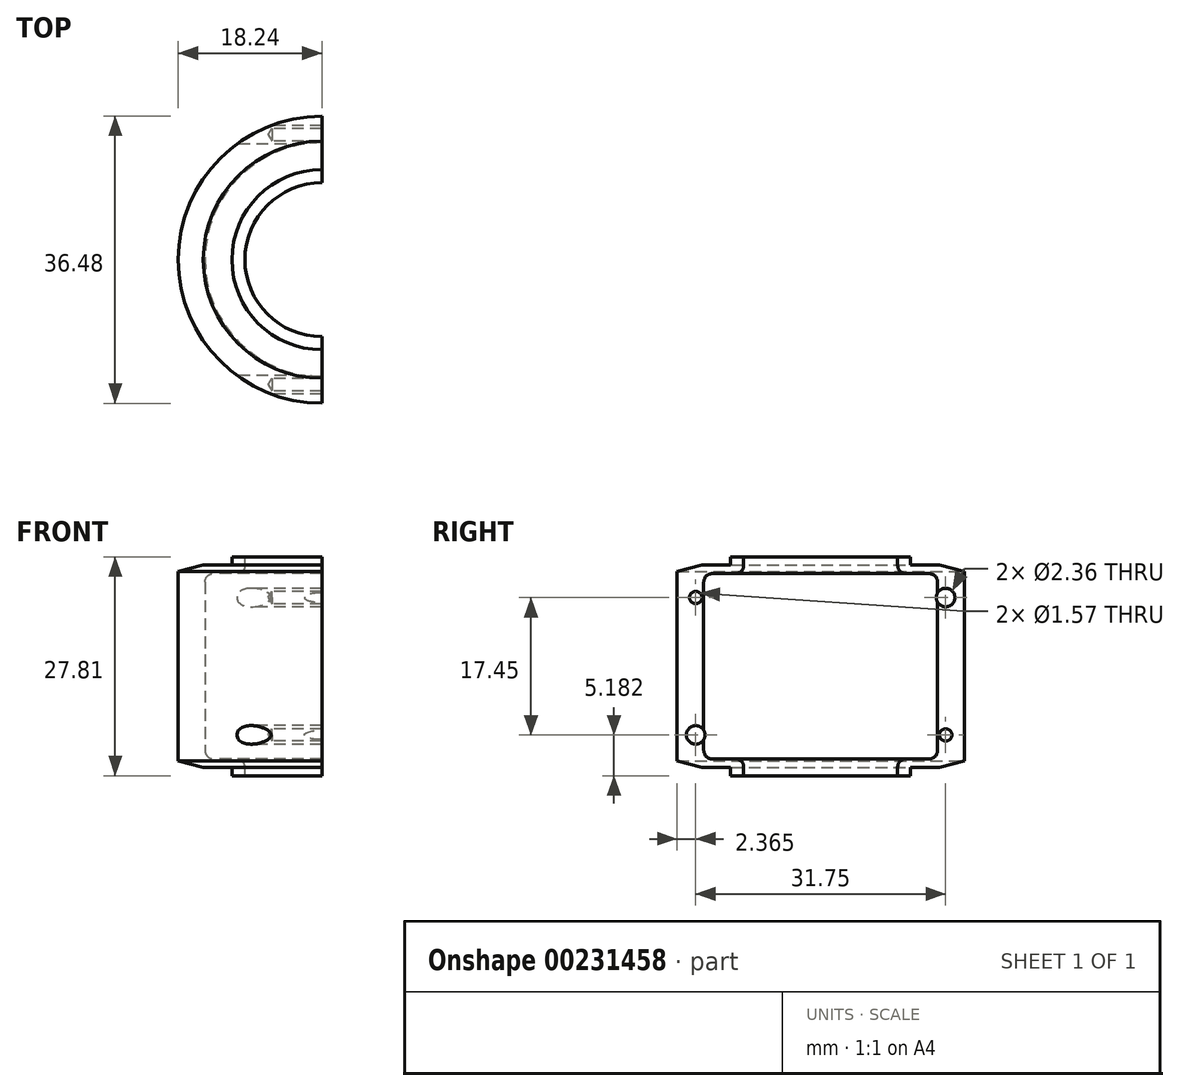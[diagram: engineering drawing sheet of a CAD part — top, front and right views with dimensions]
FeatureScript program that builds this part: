
annotation { "Feature Type Name" : "Feature", "Feature Type Description" : "" }
export const myFeature = defineFeature(function(context is Context, id is Id, definition is map)
    precondition{}
    {
        {
            var Q0;
            Q0=qCreatedBy(makeId("Right.planeOp"),FACE);
            var sketch = newSketch(context, id + "F0", { "sketchPlane" : qUnion([Q0])});
            skLineSegment(sketch, "E0", {"start": v(0, 0) * mm, "end": v(0, 2.13) * mm});
            skLineSegment(sketch, "E1", {"start": v(11.43, 0) * mm, "end": v(11.43, 1.04) * mm});
            skLineSegment(sketch, "E2", {"start": v(18.24, 1.04) * mm, "end": v(18.24, 26.77) * mm});
            skLineSegment(sketch, "E3", {"start": v(11.43, 1.04) * mm, "end": v(18.24, 1.04) * mm});
            skLineSegment(sketch, "E4", {"start": v(11.43, 26.77) * mm, "end": v(18.24, 26.77) * mm});
            skLineSegment(sketch, "E5", {"start": v(11.43, 26.77) * mm, "end": v(11.43, 27.81) * mm});
            skLineSegment(sketch, "E6", {"start": v(11.43, 27.81) * mm, "end": v(0, 27.81) * mm});
            skLineSegment(sketch, "E7", {"start": v(11.43, 0) * mm, "end": v(0, 0) * mm});
            skLineSegment(sketch, "E8", {"start": v(0, 2.13) * mm, "end": v(14.86, 2.13) * mm});
            skLineSegment(sketch, "E9", {"start": v(14.86, 2.13) * mm, "end": v(14.86, 25.68) * mm});
            skLineSegment(sketch, "E10", {"start": v(14.86, 25.68) * mm, "end": v(0, 25.68) * mm});
            skLineSegment(sketch, "E11.trimOffspring", {"start": v(0, 25.68) * mm, "end": v(0, 27.81) * mm});
            skSolve(sketch);
        }
        {
            var Q0;
            Q0=makeQuery(id+"F0.imprint","IMPRINT",FACE,{"disambiguationData":[TD([[makeQuery(id+"F0.imprint","IMPRINT",EDGE,{"derivedFrom":sQuery(id+"F0.wireOp",EDGE,"E0")}),-1.0]])]});
            var Q1;
            Q1=sQuery(id+"F0.wireOp",EDGE,"E11.trimOffspring");
            revolve(context, id + "F1", {"entities" : qUnion([Q0]), "axis" : qUnion([Q1]), "revolveType" : RevolveType.ONE_DIRECTION, "angle" : 180 * degree});
        }
        {
            var Q0;
            Q0=makeQuery(id+"F1.opRevolve","SWEPT_FACE",FACE,{"disambiguationData":[OSD([sQuery(id+"F0.wireOp",EDGE,"E6")])]});
            var sketch = newSketch(context, id + "F2", { "sketchPlane" : qUnion([Q0])});
            skCircle(sketch, "E12", {"center": v(0, 0) * mm, "radius": 9.78 * mm});
            skSolve(sketch);
        }
        {
            var Q0;
            {var subQ0=sQuery(id+"F2.wireOp",EDGE,"E12");var subQ1=makeQuery(id+"F1.opRevolve","CAP_EDGE",EDGE,{"disambiguationData":[OSD([sQuery(id+"F0.wireOp",EDGE,"E6")])],"isStart":false});var subQ2=makeQuery(id+"F2.imprint","INTERSECT",VERTEX,{"disambiguationData":[OD(0.0)],"derivedFrom":[subQ1,subQ0]});Q0=makeQuery(id+"F2.imprint","IMPRINT",FACE,{"disambiguationData":[TD([[makeQuery(id+"F2.imprint","IMPRINT",EDGE,{"disambiguationData":[TD([[subQ2,-1.0]])],"derivedFrom":subQ0}),1.0]])]});}
            var Q1;
            {var subQ0=sQuery(id+"F2.wireOp",EDGE,"E12");var subQ1=makeQuery(id+"F1.opRevolve","CAP_EDGE",EDGE,{"disambiguationData":[OSD([sQuery(id+"F0.wireOp",EDGE,"E6")])],"isStart":false});var subQ2=makeQuery(id+"F2.imprint","INTERSECT",VERTEX,{"disambiguationData":[OD(0.0)],"derivedFrom":[subQ1,subQ0]});Q1=makeQuery(id+"F2.imprint","IMPRINT",FACE,{"disambiguationData":[TD([[makeQuery(id+"F2.imprint","IMPRINT",EDGE,{"disambiguationData":[TD([[subQ2,1.0]])],"derivedFrom":subQ0}),1.0]])]});}
            extrude(context, id + "F3", {"entities" : qUnion([Q0, Q1]), "operationType" : NewBodyOperationType.REMOVE, "oppositeDirection" : true, "depth" : 27.8 * mm});
        }
        {
            var Q0;
            Q0=makeQuery(id+"F3.boolean.opBoolean","COPY",EDGE,{"derivedFrom":makeQuery(id+"F3.opExtrude","CAP_EDGE",EDGE,{"disambiguationData":[OSD([sQuery(id+"F2.wireOp",EDGE,"E12")])],"isStart":true})});
            var Q1;
            Q1=makeQuery(id+"F3.boolean.opBoolean","INTERSECT",EDGE,{"derivedFrom":[makeQuery(id+"F1.opRevolve","SWEPT_FACE",FACE,{"disambiguationData":[OSD([sQuery(id+"F0.wireOp",EDGE,"E10")])]}),makeQuery(id+"F3.opExtrude","SWEPT_FACE",FACE,{"disambiguationData":[OSD([sQuery(id+"F2.wireOp",EDGE,"E12")])]})]});
            var Q2;
            Q2=makeQuery(id+"F3.boolean.opBoolean","INTERSECT",EDGE,{"derivedFrom":[makeQuery(id+"F1.opRevolve","SWEPT_FACE",FACE,{"disambiguationData":[OSD([sQuery(id+"F0.wireOp",EDGE,"E8")])]}),makeQuery(id+"F3.opExtrude","SWEPT_FACE",FACE,{"disambiguationData":[OSD([sQuery(id+"F2.wireOp",EDGE,"E12")])]})]});
            var Q3;
            Q3=makeQuery(id+"F3.boolean.opBoolean","COPY",EDGE,{"derivedFrom":makeQuery(id+"F3.opExtrude","CAP_EDGE",EDGE,{"disambiguationData":[OSD([sQuery(id+"F2.wireOp",EDGE,"E12")])],"isStart":false})});
            fillet(context, id + "F4", {"entities" : qUnion([Q0, Q1, Q2, Q3]), "radius" : 1.02 * mm, "tangentPropagation" : true, "allowEdgeOverflow" : false});
        }
        {
            var Q0;
            Q0=makeQuery(id+"F1.opRevolve","SWEPT_EDGE",EDGE,{"disambiguationData":[OSD([sQuery(id+"F0.wireOp",EDGE,"E9"),sQuery(id+"F0.wireOp",EDGE,"E10")])]});
            var Q1;
            Q1=makeQuery(id+"F1.opRevolve","SWEPT_EDGE",EDGE,{"disambiguationData":[OSD([sQuery(id+"F0.wireOp",EDGE,"E8"),sQuery(id+"F0.wireOp",EDGE,"E9")])]});
            fillet(context, id + "F5", {"entities" : qUnion([Q0, Q1]), "radius" : 1.1 * mm, "tangentPropagation" : true, "allowEdgeOverflow" : false});
        }
        {
            var Q0;
            Q0=makeQuery(id+"F3.boolean.opBoolean","SPLIT",FACE,{"disambiguationData":[OD(0.0)],"derivedFrom":makeQuery(id+"F1.opRevolve","CAP_FACE",FACE,{"disambiguationData":[OSD([sQuery(id+"F0.wireOp",EDGE,"E0"),sQuery(id+"F0.wireOp",EDGE,"E1"),sQuery(id+"F0.wireOp",EDGE,"E2"),sQuery(id+"F0.wireOp",EDGE,"E3"),sQuery(id+"F0.wireOp",EDGE,"E4"),sQuery(id+"F0.wireOp",EDGE,"E5"),sQuery(id+"F0.wireOp",EDGE,"E6"),sQuery(id+"F0.wireOp",EDGE,"E7"),sQuery(id+"F0.wireOp",EDGE,"E8"),sQuery(id+"F0.wireOp",EDGE,"E9"),sQuery(id+"F0.wireOp",EDGE,"E10"),sQuery(id+"F0.wireOp",EDGE,"E11.trimOffspring")])],"isStart":false})});
            var sketch = newSketch(context, id + "F6", { "sketchPlane" : qUnion([Q0])});
            skPoint(sketch, "E13.startSnap0", {"position": v(18.24, 13.9) * mm});
            skPoint(sketch, "E14", {"position": v(15.88, 22.63) * mm});
            skPoint(sketch, "E15", {"position": v(15.88, 5.18) * mm});
            skPoint(sketch, "E16", {"position": v(-15.88, 5.18) * mm});
            skPoint(sketch, "E17", {"position": v(-15.88, 22.63) * mm});
            skSolve(sketch);
        }
        {
            var Q0;
            Q0=sQuery(id+"F6.wireOp",VERTEX,"E14");
            var Q1;
            Q1=sQuery(id+"F6.wireOp",VERTEX,"E16");
            var Q2;
            Q2=makeQuery(id+"F1.opRevolve","SWEPT_BODY",BODY,{"disambiguationData":[OSD([sQuery(id+"F0.wireOp",EDGE,"E0"),sQuery(id+"F0.wireOp",EDGE,"E1"),sQuery(id+"F0.wireOp",EDGE,"E2"),sQuery(id+"F0.wireOp",EDGE,"E3"),sQuery(id+"F0.wireOp",EDGE,"E4"),sQuery(id+"F0.wireOp",EDGE,"E5"),sQuery(id+"F0.wireOp",EDGE,"E6"),sQuery(id+"F0.wireOp",EDGE,"E7"),sQuery(id+"F0.wireOp",EDGE,"E8"),sQuery(id+"F0.wireOp",EDGE,"E9"),sQuery(id+"F0.wireOp",EDGE,"E10"),sQuery(id+"F0.wireOp",EDGE,"E11.trimOffspring")])]});
            hole(context, id + "F7", {"style" : HoleStyle.SIMPLE, "endStyle" : HoleEndStyle.THROUGH, "holeDiameter" : 2.36 * mm, "majorDiameter" : 6.35 * mm, "locations" : qUnion([Q0, Q1]), "scope" : qUnion([Q2]), "isTappedThrough" : true, "tappedDepth" : 12.7 * mm, "tapClearance" : 3});
        }
        {
            var Q0;
            Q0=sQuery(id+"F6.wireOp",VERTEX,"E15");
            var Q1;
            Q1=sQuery(id+"F6.wireOp",VERTEX,"E17");
            var Q2;
            Q2=makeQuery(id+"F1.opRevolve","SWEPT_BODY",BODY,{"disambiguationData":[OSD([sQuery(id+"F0.wireOp",EDGE,"E0"),sQuery(id+"F0.wireOp",EDGE,"E1"),sQuery(id+"F0.wireOp",EDGE,"E2"),sQuery(id+"F0.wireOp",EDGE,"E3"),sQuery(id+"F0.wireOp",EDGE,"E4"),sQuery(id+"F0.wireOp",EDGE,"E5"),sQuery(id+"F0.wireOp",EDGE,"E6"),sQuery(id+"F0.wireOp",EDGE,"E7"),sQuery(id+"F0.wireOp",EDGE,"E8"),sQuery(id+"F0.wireOp",EDGE,"E9"),sQuery(id+"F0.wireOp",EDGE,"E10"),sQuery(id+"F0.wireOp",EDGE,"E11.trimOffspring")])]});
            hole(context, id + "F8", {"style" : HoleStyle.SIMPLE, "endStyle" : HoleEndStyle.BLIND, "holeDiameter" : 1.57 * mm, "majorDiameter" : 6.35 * mm, "holeDepth" : 6.35 * mm, "locations" : qUnion([Q0, Q1]), "scope" : qUnion([Q2]), "isTappedThrough" : true, "tappedDepth" : 12.7 * mm, "tapClearance" : 3});
        }
        {
            var Q0;
            Q0=makeQuery(id+"F1.opRevolve","SWEPT_EDGE",EDGE,{"disambiguationData":[OSD([sQuery(id+"F0.wireOp",EDGE,"E2"),sQuery(id+"F0.wireOp",EDGE,"E3")])]});
            var Q1;
            Q1=makeQuery(id+"F1.opRevolve","SWEPT_EDGE",EDGE,{"disambiguationData":[OSD([sQuery(id+"F0.wireOp",EDGE,"E2"),sQuery(id+"F0.wireOp",EDGE,"E4")])]});
            chamfer(context, id + "F9", {"entities" : qUnion([Q0, Q1]), "chamferType" : ChamferType.OFFSET_ANGLE, "width" : 3.17 * mm, "oppositeDirection" : false, "angle" : 15 * degree, "tangentPropagation" : true});
        }
    });
